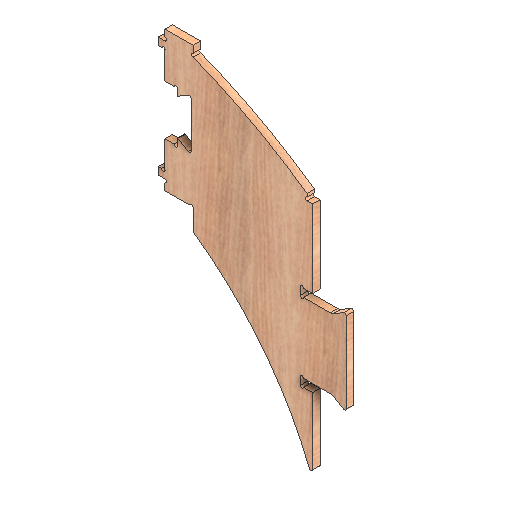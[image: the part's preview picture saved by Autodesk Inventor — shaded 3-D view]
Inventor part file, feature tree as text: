
AUTODESK INVENTOR PART (.ipt)
format: ipt  version: 2021 (Build 250183000, 183)  size: 251,392 bytes
history: native  units: mm
features: other x2, extrude x1
ambient origin geometry x8: Origin, YZ Plane, XZ Plane, XY Plane, X Axis, Y Axis, Z Axis, Center Point
bodies: Solid1 (feature_tree)
feature tree (3):
  other  "CONTOURS"
  other  "LETTERS"
  extrude  "Extrusion1"  Depth=18.0mm TaperAngle=0.0deg
